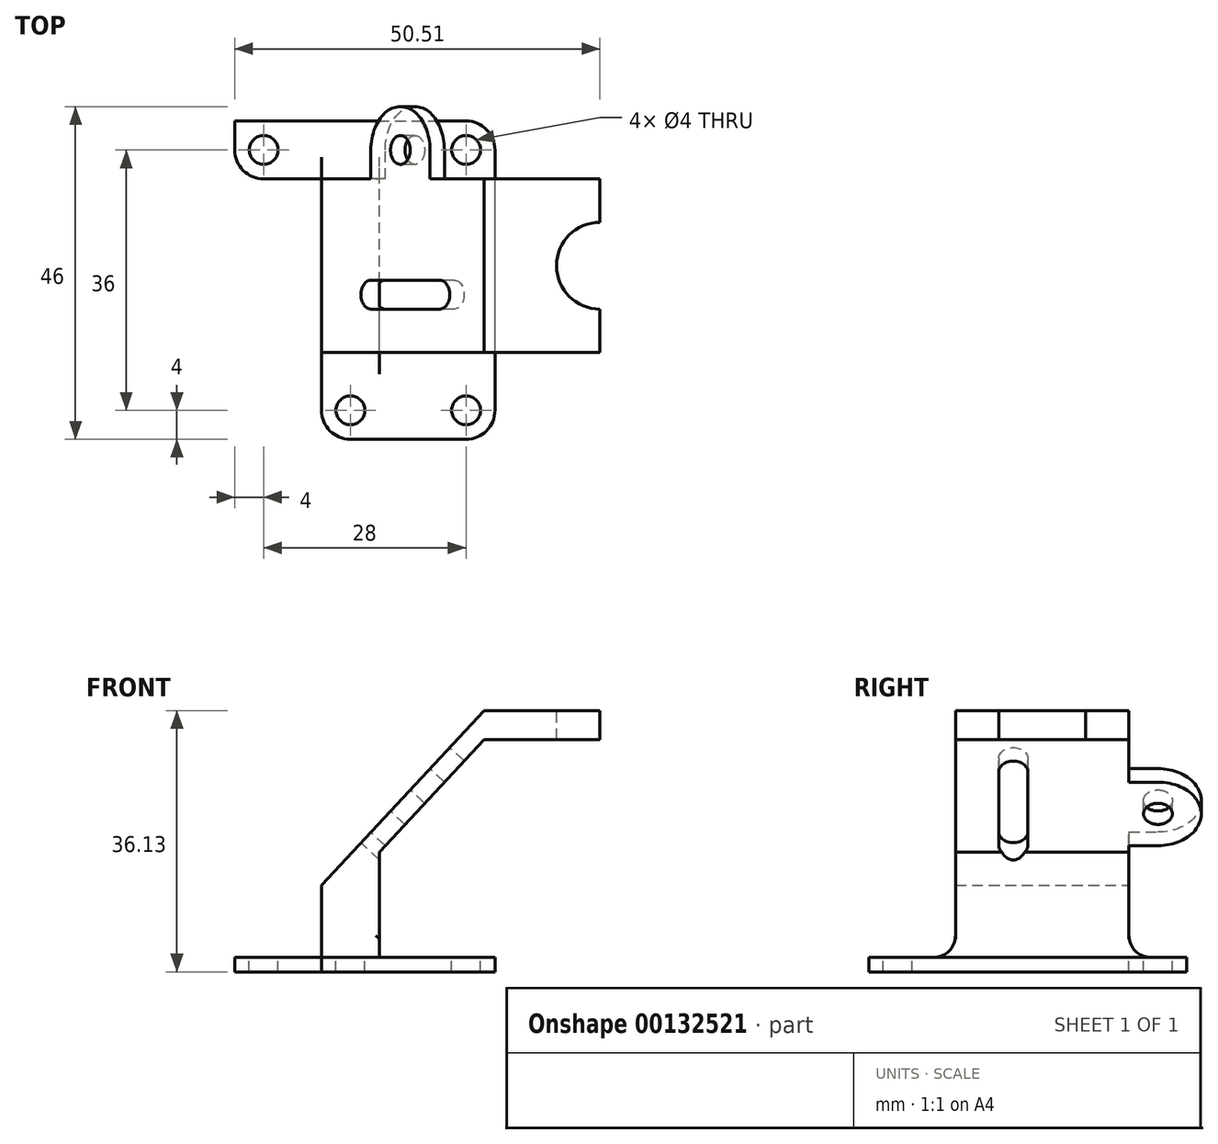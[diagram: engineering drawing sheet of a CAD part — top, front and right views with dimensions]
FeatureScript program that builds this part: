
annotation { "Feature Type Name" : "Feature", "Feature Type Description" : "" }
export const myFeature = defineFeature(function(context is Context, id is Id, definition is map)
    precondition{}
    {
        {
            var Q0;
            Q0=qCreatedBy(makeId("Front.planeOp"),FACE);
            var sketch = newSketch(context, id + "F0", { "sketchPlane" : qUnion([Q0])});
            skLineSegment(sketch, "E0.bottom", {"start": v(0, 0) * mm, "end": v(36, 0) * mm});
            skLineSegment(sketch, "E0.left", {"start": v(0, 0) * mm, "end": v(0, 2) * mm});
            skLineSegment(sketch, "E0.right", {"start": v(36, 0) * mm, "end": v(36, 2) * mm});
            skLineSegment(sketch, "E1", {"start": v(12, 2) * mm, "end": v(12, 12) * mm});
            skLineSegment(sketch, "E2", {"start": v(12, 12) * mm, "end": v(34.5, 36.13) * mm});
            skLineSegment(sketch, "E3", {"start": v(34.5, 36.13) * mm, "end": v(50.5, 36.13) * mm});
            skLineSegment(sketch, "E4", {"start": v(50.5, 36.13) * mm, "end": v(50.5, 32.13) * mm});
            skLineSegment(sketch, "E5", {"start": v(50.5, 32.13) * mm, "end": v(34.5, 32.13) * mm});
            skLineSegment(sketch, "E6", {"start": v(34.5, 32.13) * mm, "end": v(20, 16.58) * mm});
            skLineSegment(sketch, "E7", {"start": v(20, 16.58) * mm, "end": v(20, 2) * mm});
            skLineSegment(sketch, "E8", {"start": v(0, 2) * mm, "end": v(12, 2) * mm});
            skLineSegment(sketch, "E9", {"start": v(12, 2) * mm, "end": v(20, 2) * mm});
            skLineSegment(sketch, "E10", {"start": v(20, 2) * mm, "end": v(36, 2) * mm});
            skLineSegment(sketch, "E11", {"start": v(20, 16.58) * mm, "end": v(41.33, 16.58) * mm, "construction": true});
            skSolve(sketch);
        }
        {
            var Q0;
            Q0 = qSketchRegion(id + "F0", true);
            extrude(context, id + "F1", {"entities" : qUnion([Q0]), "depth" : 44 * mm});
        }
        {
            var Q0;
            Q0=makeQuery(id+"F1.opExtrude","SWEPT_FACE",FACE,{"disambiguationData":[OSD([sQuery(id+"F0.wireOp",EDGE,"E3")])]});
            var sketch = newSketch(context, id + "F2", { "sketchPlane" : qUnion([Q0])});
            skArc(sketch, "E12", {"start": v(50.5, -14) * mm, "mid": v(44.5, -20) * mm, "end": v(50.5, -26) * mm});
            skLineSegment(sketch, "E13", {"start": v(50.5, -8) * mm, "end": v(34.5, -8) * mm});
            skLineSegment(sketch, "E14", {"start": v(50.5, -32) * mm, "end": v(34.5, -32) * mm});
            skLineSegment(sketch, "E15", {"start": v(34.5, -8) * mm, "end": v(34.5, -32) * mm});
            skSolve(sketch);
        }
        {
            var Q0;
            {var subQ0=sQuery(id+"F2.wireOp",EDGE,"E12");Q0=makeQuery(id+"F2.imprint","IMPRINT",FACE,{"disambiguationData":[TD([[makeQuery(id+"F2.imprint","IMPRINT",EDGE,{"derivedFrom":subQ0}),1.0]])]});}
            var Q1;
            {var subQ0=sQuery(id+"F2.wireOp",EDGE,"E14");Q1=makeQuery(id+"F2.imprint","IMPRINT",FACE,{"disambiguationData":[TD([[makeQuery(id+"F2.imprint","IMPRINT",EDGE,{"derivedFrom":subQ0}),1.0]])]});}
            var Q2;
            {var subQ0=sQuery(id+"F2.wireOp",EDGE,"E13");Q2=makeQuery(id+"F2.imprint","IMPRINT",FACE,{"disambiguationData":[TD([[makeQuery(id+"F2.imprint","IMPRINT",EDGE,{"derivedFrom":subQ0}),-1.0]])]});}
            extrude(context, id + "F3", {"entities" : qUnion([Q0, Q1, Q2]), "operationType" : NewBodyOperationType.REMOVE, "endBound" : BoundingType.UP_TO_NEXT, "oppositeDirection" : true, "depth" : 25 * mm});
        }
        {
            var Q0;
            Q0=makeQuery(id+"F1.opExtrude","SWEPT_FACE",FACE,{"disambiguationData":[OSD([sQuery(id+"F0.wireOp",EDGE,"E2")])]});
            var sketch = newSketch(context, id + "F4", { "sketchPlane" : qUnion([Q0])});
            skLineSegment(sketch, "E16", {"start": v(26, 40.96) * mm, "end": v(26, 26.96) * mm});
            skLineSegment(sketch, "E17.0", {"start": v(22, 40.96) * mm, "end": v(22, 26.96) * mm});
            skArc(sketch, "E18", {"start": v(26, 40.96) * mm, "mid": v(24, 42.96) * mm, "end": v(22, 40.96) * mm});
            skArc(sketch, "E19", {"start": v(22, 26.96) * mm, "mid": v(24, 24.96) * mm, "end": v(26, 26.96) * mm});
            skLineSegment(sketch, "E20", {"start": v(8, 49.96) * mm, "end": v(8, 16.96) * mm});
            skLineSegment(sketch, "E21", {"start": v(8, 16.96) * mm, "end": v(0, 16.96) * mm});
            skLineSegment(sketch, "E22", {"start": v(0, 49.96) * mm, "end": v(8, 49.96) * mm});
            skLineSegment(sketch, "E23", {"start": v(32, 49.96) * mm, "end": v(32, 16.96) * mm});
            skLineSegment(sketch, "E24", {"start": v(8, 38.96) * mm, "end": v(4, 38.96) * mm});
            skLineSegment(sketch, "E25", {"start": v(8, 26.96) * mm, "end": v(4, 26.96) * mm});
            skArc(sketch, "E26", {"start": v(4, 38.96) * mm, "mid": v(-2, 32.96) * mm, "end": v(4, 26.96) * mm});
            skCircle(sketch, "E27", {"center": v(4, 32.96) * mm, "radius": 2 * mm});
            skSolve(sketch);
        }
        {
            var Q0;
            Q0=makeQuery(id+"F4.imprint","IMPRINT",FACE,{"disambiguationData":[TD([[makeQuery(id+"F4.imprint","IMPRINT",EDGE,{"derivedFrom":sQuery(id+"F4.wireOp",EDGE,"E16")}),-1.0]])]});
            var Q1;
            {var subQ5=sQuery(id+"F4.wireOp",EDGE,"E22");Q1=makeQuery(id+"F4.imprint","IMPRINT",FACE,{"disambiguationData":[TD([[makeQuery(id+"F4.imprint","IMPRINT",EDGE,{"derivedFrom":subQ5}),1.0]])]});}
            var Q2;
            {var subQ5=sQuery(id+"F4.wireOp",EDGE,"E21");Q2=makeQuery(id+"F4.imprint","IMPRINT",FACE,{"disambiguationData":[TD([[makeQuery(id+"F4.imprint","IMPRINT",EDGE,{"derivedFrom":subQ5}),-1.0]])]});}
            var Q3;
            {var subQ0=sQuery(id+"F4.wireOp",EDGE,"E23");Q3=makeQuery(id+"F4.imprint","IMPRINT",FACE,{"disambiguationData":[TD([[makeQuery(id+"F4.imprint","IMPRINT",EDGE,{"derivedFrom":subQ0}),1.0]])]});}
            var Q4;
            Q4=makeQuery(id+"F4.imprint","IMPRINT",FACE,{"disambiguationData":[TD([[makeQuery(id+"F4.imprint","IMPRINT",EDGE,{"derivedFrom":sQuery(id+"F4.wireOp",EDGE,"E27")}),1.0]])]});
            extrude(context, id + "F5", {"entities" : qUnion([Q0, Q1, Q2, Q3, Q4]), "operationType" : NewBodyOperationType.REMOVE, "endBound" : BoundingType.UP_TO_NEXT, "oppositeDirection" : true, "depth" : 25 * mm});
        }
        {
            var Q0;
            Q0=makeQuery(id+"F1.opExtrude","SWEPT_FACE",FACE,{"disambiguationData":[OSD([sQuery(id+"F0.wireOp",EDGE,"E1")])]});
            var sketch = newSketch(context, id + "F6", { "sketchPlane" : qUnion([Q0])});
            skLineSegment(sketch, "E28", {"start": v(8, 12) * mm, "end": v(32, 12) * mm});
            skLineSegment(sketch, "E29", {"start": v(32, 12) * mm, "end": v(32, 2) * mm});
            skLineSegment(sketch, "E30", {"start": v(32, 2) * mm, "end": v(8, 2) * mm});
            skLineSegment(sketch, "E31", {"start": v(8, 2) * mm, "end": v(8, 12) * mm});
            skLineSegment(sketch, "E32", {"start": v(0, 2) * mm, "end": v(8, 2) * mm});
            skLineSegment(sketch, "E33", {"start": v(32, 2) * mm, "end": v(44, 2) * mm});
            skLineSegment(sketch, "E34", {"start": v(8, 12) * mm, "end": v(0, 12) * mm});
            skLineSegment(sketch, "E35", {"start": v(0, 12) * mm, "end": v(0, 2) * mm});
            skLineSegment(sketch, "E36", {"start": v(32, 12) * mm, "end": v(44, 12) * mm});
            skLineSegment(sketch, "E37", {"start": v(44, 12) * mm, "end": v(44, 2) * mm});
            skArc(sketch, "E38", {"start": v(5, 2) * mm, "mid": v(7.12, 2.88) * mm, "end": v(8, 5) * mm});
            skArc(sketch, "E39", {"start": v(32, 5) * mm, "mid": v(32.88, 2.88) * mm, "end": v(35, 2) * mm});
            skSolve(sketch);
        }
        {
            var Q0;
            {var subQ0=sQuery(id+"F6.wireOp",EDGE,"E34");Q0=makeQuery(id+"F6.imprint","IMPRINT",FACE,{"disambiguationData":[TD([[makeQuery(id+"F6.imprint","IMPRINT",EDGE,{"derivedFrom":subQ0}),1.0]])]});}
            var Q1;
            {var subQ3=sQuery(id+"F6.wireOp",EDGE,"E36");Q1=makeQuery(id+"F6.imprint","IMPRINT",FACE,{"disambiguationData":[TD([[makeQuery(id+"F6.imprint","IMPRINT",EDGE,{"derivedFrom":subQ3}),1.0]])]});}
            extrude(context, id + "F7", {"entities" : qUnion([Q0, Q1]), "operationType" : NewBodyOperationType.REMOVE, "endBound" : BoundingType.THROUGH_ALL, "oppositeDirection" : true, "depth" : 25 * mm});
        }
        {
            var Q0;
            Q0=makeQuery(id+"F7.boolean.opBoolean","MERGE",FACE,{"derivedFrom":[makeQuery(id+"F1.opExtrude","SWEPT_FACE",FACE,{"disambiguationData":[OSD([sQuery(id+"F0.wireOp",EDGE,"E8")])]}),makeQuery(id+"F1.opExtrude","SWEPT_FACE",FACE,{"disambiguationData":[OSD([sQuery(id+"F0.wireOp",EDGE,"E10")])]}),makeQuery(id+"F7.opExtrude","SWEPT_FACE",FACE,{"disambiguationData":[OSD([sQuery(id+"F6.wireOp",EDGE,"E32")])]}),makeQuery(id+"F7.opExtrude","SWEPT_FACE",FACE,{"disambiguationData":[OSD([sQuery(id+"F6.wireOp",EDGE,"E33")])]})]});
            var sketch = newSketch(context, id + "F8", { "sketchPlane" : qUnion([Q0])});
            skLineSegment(sketch, "E40.0", {"start": v(0, 0) * mm, "end": v(36, 0) * mm});
            skLineSegment(sketch, "E41.0", {"start": v(0, -44) * mm, "end": v(0, 0) * mm});
            skLineSegment(sketch, "E42.0.0", {"start": v(36, 0) * mm, "end": v(0, 0) * mm});
            skLineSegment(sketch, "E43.0", {"start": v(12, -32) * mm, "end": v(12, -8) * mm});
            skLineSegment(sketch, "E44", {"start": v(12, -8) * mm, "end": v(12, 0) * mm});
            skLineSegment(sketch, "E45", {"start": v(0, 0) * mm, "end": v(0, -44) * mm});
            skArc(sketch, "E46", {"start": v(12, -40) * mm, "mid": v(13.17, -42.83) * mm, "end": v(16, -44) * mm});
            skArc(sketch, "E47", {"start": v(32, -44) * mm, "mid": v(34.83, -42.83) * mm, "end": v(36, -40) * mm});
            skArc(sketch, "E48", {"start": v(36, -4) * mm, "mid": v(34.83, -1.17) * mm, "end": v(32, 0) * mm});
            skLineSegment(sketch, "E49", {"start": v(12, -8) * mm, "end": v(0, -8) * mm});
            skLineSegment(sketch, "E50", {"start": v(0, -8) * mm, "end": v(0, -44) * mm});
            skLineSegment(sketch, "E51", {"start": v(12, -35) * mm, "end": v(12, -32) * mm});
            skLineSegment(sketch, "E52", {"start": v(12, -8) * mm, "end": v(12, -5) * mm});
            skLineSegment(sketch, "E53", {"start": v(12, -5) * mm, "end": v(12, 0) * mm});
            skLineSegment(sketch, "E54", {"start": v(12, -8) * mm, "end": v(12, -32) * mm});
            skLineSegment(sketch, "E55", {"start": v(12, -44) * mm, "end": v(16, -44) * mm});
            skLineSegment(sketch, "E56", {"start": v(32, -44) * mm, "end": v(36, -44) * mm});
            skLineSegment(sketch, "E57", {"start": v(36, -44) * mm, "end": v(36, -40) * mm});
            skLineSegment(sketch, "E58", {"start": v(36, -4) * mm, "end": v(36, 0) * mm});
            skLineSegment(sketch, "E59", {"start": v(36, -4) * mm, "end": v(36, -40) * mm});
            skLineSegment(sketch, "E60", {"start": v(16, -44) * mm, "end": v(32, -44) * mm});
            skLineSegment(sketch, "E61", {"start": v(12, -35) * mm, "end": v(12, -44) * mm});
            skLineSegment(sketch, "E62", {"start": v(12, 0) * mm, "end": v(4, 0) * mm});
            skLineSegment(sketch, "E63", {"start": v(12, -8) * mm, "end": v(4, -8) * mm});
            skPoint(sketch, "E63.endSnap0", {"position": v(6, -8) * mm});
            skLineSegment(sketch, "E64", {"start": v(4, 0) * mm, "end": v(4, -8) * mm, "construction": true});
            skArc(sketch, "E65", {"start": v(4, 0) * mm, "mid": v(0, -4) * mm, "end": v(4, -8) * mm});
            skCircle(sketch, "E66", {"center": v(4, -4) * mm, "radius": 2 * mm});
            skCircle(sketch, "E67", {"center": v(16, -40) * mm, "radius": 2 * mm});
            skCircle(sketch, "E68", {"center": v(32, -40) * mm, "radius": 2 * mm});
            skCircle(sketch, "E69", {"center": v(32, -4) * mm, "radius": 2 * mm});
            skSolve(sketch);
        }
        {
            var Q0;
            {var subQ0=sQuery(id+"F8.wireOp",EDGE,"E49");Q0=makeQuery(id+"F8.imprint","IMPRINT",FACE,{"disambiguationData":[TD([[makeQuery(id+"F8.imprint","IMPRINT",EDGE,{"derivedFrom":subQ0}),-1.0]])]});}
            var Q1;
            {var subQ0=sQuery(id+"F8.wireOp",EDGE,"E45");var subQ1=sQuery(id+"F8.wireOp",EDGE,"E42.0.0");var subQ2=makeQuery(id+"F8.imprint","INTERSECT",VERTEX,{"derivedFrom":[subQ1,subQ0]});Q1=makeQuery(id+"F8.imprint","IMPRINT",FACE,{"disambiguationData":[TD([[makeQuery(id+"F8.imprint","IMPRINT",EDGE,{"disambiguationData":[TD([[subQ2,1.0]])],"derivedFrom":subQ0}),-1.0]])]});}
            var Q2;
            Q2=makeQuery(id+"F8.imprint","IMPRINT",FACE,{"disambiguationData":[TD([[makeQuery(id+"F8.imprint","IMPRINT",EDGE,{"derivedFrom":sQuery(id+"F8.wireOp",EDGE,"E49")}),1.0]])]});
            var Q3;
            {var subQ2=sQuery(id+"F8.wireOp",EDGE,"E48");Q3=makeQuery(id+"F8.imprint","IMPRINT",FACE,{"disambiguationData":[TD([[makeQuery(id+"F8.imprint","IMPRINT",EDGE,{"derivedFrom":subQ2}),-1.0]])]});}
            var Q4;
            Q4=makeQuery(id+"F8.imprint","IMPRINT",FACE,{"disambiguationData":[TD([[makeQuery(id+"F8.imprint","IMPRINT",EDGE,{"derivedFrom":sQuery(id+"F8.wireOp",EDGE,"E69")}),1.0]])]});
            var Q5;
            Q5=makeQuery(id+"F8.imprint","IMPRINT",FACE,{"disambiguationData":[TD([[makeQuery(id+"F8.imprint","IMPRINT",EDGE,{"derivedFrom":sQuery(id+"F8.wireOp",EDGE,"E68")}),1.0]])]});
            var Q6;
            Q6=makeQuery(id+"F8.imprint","IMPRINT",FACE,{"disambiguationData":[TD([[makeQuery(id+"F8.imprint","IMPRINT",EDGE,{"derivedFrom":sQuery(id+"F8.wireOp",EDGE,"E47")}),-1.0]])]});
            var Q7;
            {var subQ0=sQuery(id+"F8.wireOp",EDGE,"E46");Q7=makeQuery(id+"F8.imprint","IMPRINT",FACE,{"disambiguationData":[TD([[makeQuery(id+"F8.imprint","IMPRINT",EDGE,{"derivedFrom":subQ0}),-1.0]])]});}
            var Q8;
            Q8=makeQuery(id+"F8.imprint","IMPRINT",FACE,{"disambiguationData":[TD([[makeQuery(id+"F8.imprint","IMPRINT",EDGE,{"derivedFrom":sQuery(id+"F8.wireOp",EDGE,"E67")}),1.0]])]});
            var Q9;
            Q9=makeQuery(id+"F8.imprint","IMPRINT",FACE,{"disambiguationData":[TD([[makeQuery(id+"F8.imprint","IMPRINT",EDGE,{"derivedFrom":sQuery(id+"F8.wireOp",EDGE,"E66")}),1.0]])]});
            extrude(context, id + "F9", {"entities" : qUnion([Q0, Q1, Q2, Q3, Q4, Q5, Q6, Q7, Q8, Q9]), "operationType" : NewBodyOperationType.REMOVE, "endBound" : BoundingType.THROUGH_ALL, "oppositeDirection" : true, "depth" : 25 * mm});
        }
        {
            var Q0;
            {var subQ0=sQuery(id+"F4.wireOp",EDGE,"E26");var subQ1=makeQuery(id+"F1.opExtrude","CAP_EDGE",EDGE,{"disambiguationData":[OSD([sQuery(id+"F0.wireOp",EDGE,"E2")])],"isStart":true});var subQ2=makeQuery(id+"F4.imprint","INTERSECT",VERTEX,{"disambiguationData":[OD(0.0)],"derivedFrom":[subQ1,subQ0]});Q0=makeQuery(id+"F4.imprint","IMPRINT",FACE,{"disambiguationData":[TD([[makeQuery(id+"F4.imprint","IMPRINT",EDGE,{"disambiguationData":[TD([[subQ2,-1.0]])],"derivedFrom":subQ0}),1.0]])]});}
            var Q1;
            Q1=makeQuery(id+"F1.opExtrude","SWEPT_FACE",FACE,{"disambiguationData":[OSD([sQuery(id+"F0.wireOp",EDGE,"E6")])]});
            extrude(context, id + "F10", {"entities" : qUnion([Q0]), "operationType" : NewBodyOperationType.ADD, "endBound" : BoundingType.UP_TO_SURFACE, "oppositeDirection" : true, "endBoundEntityFace" : qUnion([Q1]), "depth" : 25 * mm});
        }
    });
